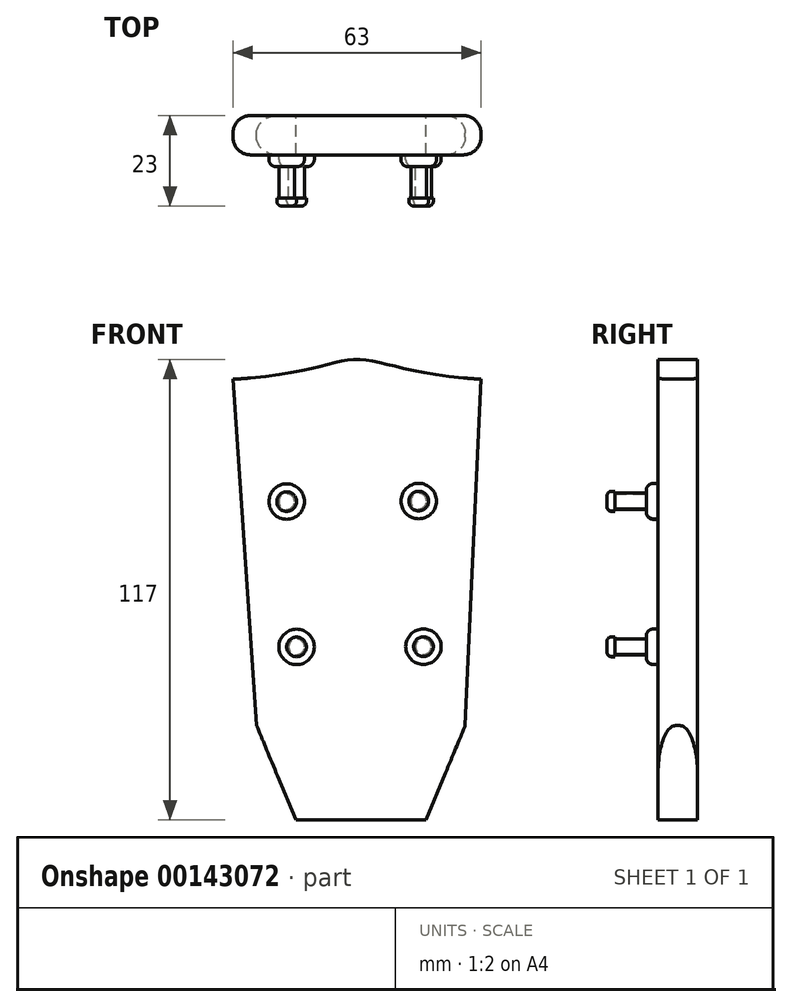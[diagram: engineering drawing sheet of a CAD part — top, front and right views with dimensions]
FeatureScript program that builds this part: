
annotation { "Feature Type Name" : "Feature", "Feature Type Description" : "" }
export const myFeature = defineFeature(function(context is Context, id is Id, definition is map)
    precondition{}
    {
        {
            var Q0;
            Q0=qCreatedBy(makeId("Front.planeOp"),FACE);
            var sketch = newSketch(context, id + "F0", { "sketchPlane" : qUnion([Q0])});
            skPoint(sketch, "E0", {"position": v(-31.5, 63.45) * mm});
            skPoint(sketch, "E1", {"position": v(31.5, 63.45) * mm});
            skPoint(sketch, "E2", {"position": v(0, 68.45) * mm});
            skPoint(sketch, "E3", {"position": v(-25.5, -24.55) * mm});
            skPoint(sketch, "E4", {"position": v(-15.5, -48.55) * mm});
            skPoint(sketch, "E5", {"position": v(17.5, -48.55) * mm});
            skPoint(sketch, "E6", {"position": v(27.5, -24.55) * mm});
            skLineSegment(sketch, "E7", {"start": v(-31.5, 63.45) * mm, "end": v(-25.5, -24.55) * mm});
            skLineSegment(sketch, "E8", {"start": v(31.5, 63.45) * mm, "end": v(27.5, -24.55) * mm});
            skLineSegment(sketch, "E9", {"start": v(-15.5, -48.55) * mm, "end": v(-25.5, -24.55) * mm});
            skLineSegment(sketch, "E10", {"start": v(27.5, -24.55) * mm, "end": v(17.5, -48.55) * mm});
            skLineSegment(sketch, "E11", {"start": v(-15.5, -48.55) * mm, "end": v(17.5, -48.55) * mm});
            skFitSpline(sketch, "E12", {"points": [v(-31.5, 63.45) * mm, v(0, 68.45) * mm, v(31.5, 63.45) * mm], "startDerivative": vector(115.04, 5.76) * mm, "endDerivative": vector(107.69, -5.76) * mm});
            skSolve(sketch);
        }
        {
            var Q0;
            Q0=makeQuery(id+"F0.imprint","IMPRINT",FACE,{"disambiguationData":[TD([[makeQuery(id+"F0.imprint","IMPRINT",EDGE,{"derivedFrom":sQuery(id+"F0.wireOp",EDGE,"E7")}),1.0]])]});
            extrude(context, id + "F1", {"entities" : qUnion([Q0]), "depth" : 10 * mm});
        }
        {
            var Q0;
            Q0=makeQuery(id+"F1.opExtrude","CAP_FACE",FACE,{"disambiguationData":[OSD([sQuery(id+"F0.wireOp",EDGE,"E7"),sQuery(id+"F0.wireOp",EDGE,"E8"),sQuery(id+"F0.wireOp",EDGE,"E9"),sQuery(id+"F0.wireOp",EDGE,"E10"),sQuery(id+"F0.wireOp",EDGE,"E11"),sQuery(id+"F0.wireOp",EDGE,"E12")])],"isStart":false});
            var sketch = newSketch(context, id + "F2", { "sketchPlane" : qUnion([Q0])});
            skCircle(sketch, "E13", {"center": v(-17.85, 32.35) * mm, "radius": 4.5 * mm});
            skPoint(sketch, "E14", {"position": v(-18.08, 64.85) * mm});
            skPoint(sketch, "E15", {"position": v(18.61, 64.85) * mm});
            skCircle(sketch, "E16", {"center": v(15.69, 32.48) * mm, "radius": 4.5 * mm});
            skCircle(sketch, "E17", {"center": v(-15.34, -4.56) * mm, "radius": 4.5 * mm});
            skCircle(sketch, "E18", {"center": v(16.9, -4.5) * mm, "radius": 4.5 * mm});
            skSolve(sketch);
        }
        {
            var Q0;
            Q0=makeQuery(id+"F2.imprint","IMPRINT",FACE,{"disambiguationData":[TD([[makeQuery(id+"F2.imprint","IMPRINT",EDGE,{"derivedFrom":sQuery(id+"F2.wireOp",EDGE,"E13")}),1.0]])]});
            var Q1;
            Q1=makeQuery(id+"F2.imprint","IMPRINT",FACE,{"disambiguationData":[TD([[makeQuery(id+"F2.imprint","IMPRINT",EDGE,{"derivedFrom":sQuery(id+"F2.wireOp",EDGE,"E16")}),1.0]])]});
            var Q2;
            Q2=makeQuery(id+"F2.imprint","IMPRINT",FACE,{"disambiguationData":[TD([[makeQuery(id+"F2.imprint","IMPRINT",EDGE,{"derivedFrom":sQuery(id+"F2.wireOp",EDGE,"E17")}),1.0]])]});
            var Q3;
            Q3=makeQuery(id+"F2.imprint","IMPRINT",FACE,{"disambiguationData":[TD([[makeQuery(id+"F2.imprint","IMPRINT",EDGE,{"derivedFrom":sQuery(id+"F2.wireOp",EDGE,"E18")}),1.0]])]});
            extrude(context, id + "F3", {"entities" : qUnion([Q0, Q1, Q2, Q3]), "operationType" : NewBodyOperationType.ADD, "depth" : 3 * mm});
        }
        {
            var Q0;
            Q0=makeQuery(id+"F3.opExtrude","CAP_EDGE",EDGE,{"disambiguationData":[OSD([sQuery(id+"F2.wireOp",EDGE,"E13")])],"isStart":false});
            var Q1;
            Q1=makeQuery(id+"F3.opExtrude","CAP_EDGE",EDGE,{"disambiguationData":[OSD([sQuery(id+"F2.wireOp",EDGE,"E16")])],"isStart":false});
            var Q2;
            Q2=makeQuery(id+"F3.opExtrude","CAP_EDGE",EDGE,{"disambiguationData":[OSD([sQuery(id+"F2.wireOp",EDGE,"E17")])],"isStart":false});
            var Q3;
            Q3=makeQuery(id+"F3.opExtrude","CAP_EDGE",EDGE,{"disambiguationData":[OSD([sQuery(id+"F2.wireOp",EDGE,"E18")])],"isStart":false});
            fillet(context, id + "F4", {"entities" : qUnion([Q0, Q1, Q2, Q3]), "radius" : 1.81 * mm, "tangentPropagation" : true, "allowEdgeOverflow" : false});
        }
        {
            var Q0;
            Q0=makeQuery(id+"F3.opExtrude","CAP_FACE",FACE,{"disambiguationData":[OSD([sQuery(id+"F2.wireOp",EDGE,"E13")])],"isStart":false});
            var sketch = newSketch(context, id + "F5", { "sketchPlane" : qUnion([Q0])});
            skCircle(sketch, "E19", {"center": v(-17.85, 32.35) * mm, "radius": 2 * mm});
            skCircle(sketch, "E20", {"center": v(15.69, 32.48) * mm, "radius": 2 * mm});
            skCircle(sketch, "E21", {"center": v(16.9, -4.5) * mm, "radius": 2 * mm});
            skCircle(sketch, "E22", {"center": v(-15.34, -4.56) * mm, "radius": 2 * mm});
            skSolve(sketch);
        }
        {
            var Q0;
            Q0=makeQuery(id+"F5.imprint","IMPRINT",FACE,{"disambiguationData":[TD([[makeQuery(id+"F5.imprint","IMPRINT",EDGE,{"derivedFrom":sQuery(id+"F5.wireOp",EDGE,"E19")}),1.0]])]});
            var Q1;
            Q1=makeQuery(id+"F5.imprint","IMPRINT",FACE,{"disambiguationData":[TD([[makeQuery(id+"F5.imprint","IMPRINT",EDGE,{"derivedFrom":sQuery(id+"F5.wireOp",EDGE,"E20")}),1.0]])]});
            var Q2;
            Q2=makeQuery(id+"F5.imprint","IMPRINT",FACE,{"disambiguationData":[TD([[makeQuery(id+"F5.imprint","IMPRINT",EDGE,{"derivedFrom":sQuery(id+"F5.wireOp",EDGE,"E22")}),1.0]])]});
            var Q3;
            Q3=makeQuery(id+"F5.imprint","IMPRINT",FACE,{"disambiguationData":[TD([[makeQuery(id+"F5.imprint","IMPRINT",EDGE,{"derivedFrom":sQuery(id+"F5.wireOp",EDGE,"E21")}),1.0]])]});
            extrude(context, id + "F6", {"entities" : qUnion([Q0, Q1, Q2, Q3]), "operationType" : NewBodyOperationType.ADD, "depth" : 8 * mm});
        }
        {
            var Q0;
            Q0=makeQuery(id+"F6.opExtrude","CAP_FACE",FACE,{"disambiguationData":[OSD([sQuery(id+"F5.wireOp",EDGE,"E22")])],"isStart":false});
            var sketch = newSketch(context, id + "F7", { "sketchPlane" : qUnion([Q0])});
            skCircle(sketch, "E23", {"center": v(-17.85, 32.35) * mm, "radius": 2.5 * mm});
            skCircle(sketch, "E24", {"center": v(15.69, 32.48) * mm, "radius": 2.5 * mm});
            skCircle(sketch, "E25", {"center": v(-15.34, -4.56) * mm, "radius": 2.5 * mm});
            skCircle(sketch, "E26", {"center": v(16.9, -4.5) * mm, "radius": 2.5 * mm});
            skSolve(sketch);
        }
        {
            var Q0;
            Q0=makeQuery(id+"F7.imprint","IMPRINT",FACE,{"disambiguationData":[TD([[makeQuery(id+"F7.imprint","IMPRINT",EDGE,{"derivedFrom":sQuery(id+"F7.wireOp",EDGE,"E26")}),1.0]])]});
            var Q1;
            Q1=makeQuery(id+"F7.imprint","IMPRINT",FACE,{"disambiguationData":[TD([[makeQuery(id+"F7.imprint","IMPRINT",EDGE,{"derivedFrom":sQuery(id+"F7.wireOp",EDGE,"E23")}),1.0]])]});
            var Q2;
            Q2=makeQuery(id+"F7.imprint","IMPRINT",FACE,{"disambiguationData":[TD([[makeQuery(id+"F7.imprint","IMPRINT",EDGE,{"derivedFrom":sQuery(id+"F7.wireOp",EDGE,"E24")}),1.0]])]});
            var Q3;
            Q3=makeQuery(id+"F7.imprint","IMPRINT",FACE,{"disambiguationData":[TD([[makeQuery(id+"F7.imprint","IMPRINT",EDGE,{"derivedFrom":sQuery(id+"F7.wireOp",EDGE,"E25")}),1.0]])]});
            var Q4;
            Q4=makeQuery(id+"F7.imprint","IMPRINT",FACE,{"disambiguationData":[TD([[makeQuery(id+"F7.imprint","IMPRINT",EDGE,{"derivedFrom":makeQuery(id+"F6.opExtrude","CAP_EDGE",EDGE,{"disambiguationData":[OSD([sQuery(id+"F5.wireOp",EDGE,"E22")])],"isStart":false})}),1.0]])]});
            extrude(context, id + "F8", {"entities" : qUnion([Q0, Q1, Q2, Q3, Q4]), "operationType" : NewBodyOperationType.ADD, "depth" : 2 * mm});
        }
        {
            var Q0;
            Q0=makeQuery(id+"F1.opExtrude","CAP_EDGE",EDGE,{"disambiguationData":[OSD([sQuery(id+"F0.wireOp",EDGE,"E7")])],"isStart":true});
            var Q1;
            Q1=makeQuery(id+"F6.opExtrude","CAP_EDGE",EDGE,{"disambiguationData":[OSD([sQuery(id+"F5.wireOp",EDGE,"E21")])],"isStart":false});
            var Q2;
            Q2=makeQuery(id+"F6.opExtrude","CAP_EDGE",EDGE,{"disambiguationData":[OSD([sQuery(id+"F5.wireOp",EDGE,"E20")])],"isStart":false});
            var Q3;
            Q3=makeQuery(id+"F6.opExtrude","CAP_EDGE",EDGE,{"disambiguationData":[OSD([sQuery(id+"F5.wireOp",EDGE,"E19")])],"isStart":false});
            var Q4;
            Q4=makeQuery(id+"F6.opExtrude","CAP_EDGE",EDGE,{"disambiguationData":[OSD([sQuery(id+"F5.wireOp",EDGE,"E22")])],"isStart":false});
            var Q5;
            Q5=makeQuery(id+"F1.opExtrude","CAP_EDGE",EDGE,{"disambiguationData":[OSD([sQuery(id+"F0.wireOp",EDGE,"E8")])],"isStart":true});
            var Q6;
            Q6=makeQuery(id+"F1.opExtrude","CAP_EDGE",EDGE,{"disambiguationData":[OSD([sQuery(id+"F0.wireOp",EDGE,"E7")])],"isStart":false});
            var Q7;
            Q7=makeQuery(id+"F1.opExtrude","CAP_EDGE",EDGE,{"disambiguationData":[OSD([sQuery(id+"F0.wireOp",EDGE,"E8")])],"isStart":false});
            fillet(context, id + "F9", {"entities" : qUnion([Q0, Q1, Q2, Q3, Q4, Q5, Q6, Q7]), "radius" : 4.47 * mm, "tangentPropagation" : true, "allowEdgeOverflow" : false});
        }
        {
            var Q0;
            Q0=makeQuery(id+"F8.opExtrude","CAP_EDGE",EDGE,{"disambiguationData":[OSD([sQuery(id+"F7.wireOp",EDGE,"E23")])],"isStart":false});
            var Q1;
            Q1=makeQuery(id+"F8.opExtrude","CAP_EDGE",EDGE,{"disambiguationData":[OSD([sQuery(id+"F7.wireOp",EDGE,"E25")])],"isStart":false});
            var Q2;
            Q2=makeQuery(id+"F8.opExtrude","CAP_EDGE",EDGE,{"disambiguationData":[OSD([sQuery(id+"F7.wireOp",EDGE,"E26")])],"isStart":false});
            var Q3;
            Q3=makeQuery(id+"F8.opExtrude","CAP_EDGE",EDGE,{"disambiguationData":[OSD([sQuery(id+"F7.wireOp",EDGE,"E24")])],"isStart":false});
            fillet(context, id + "F10", {"entities" : qUnion([Q0, Q1, Q2, Q3]), "radius" : 1.2 * mm, "tangentPropagation" : true, "allowEdgeOverflow" : false});
        }
    });
